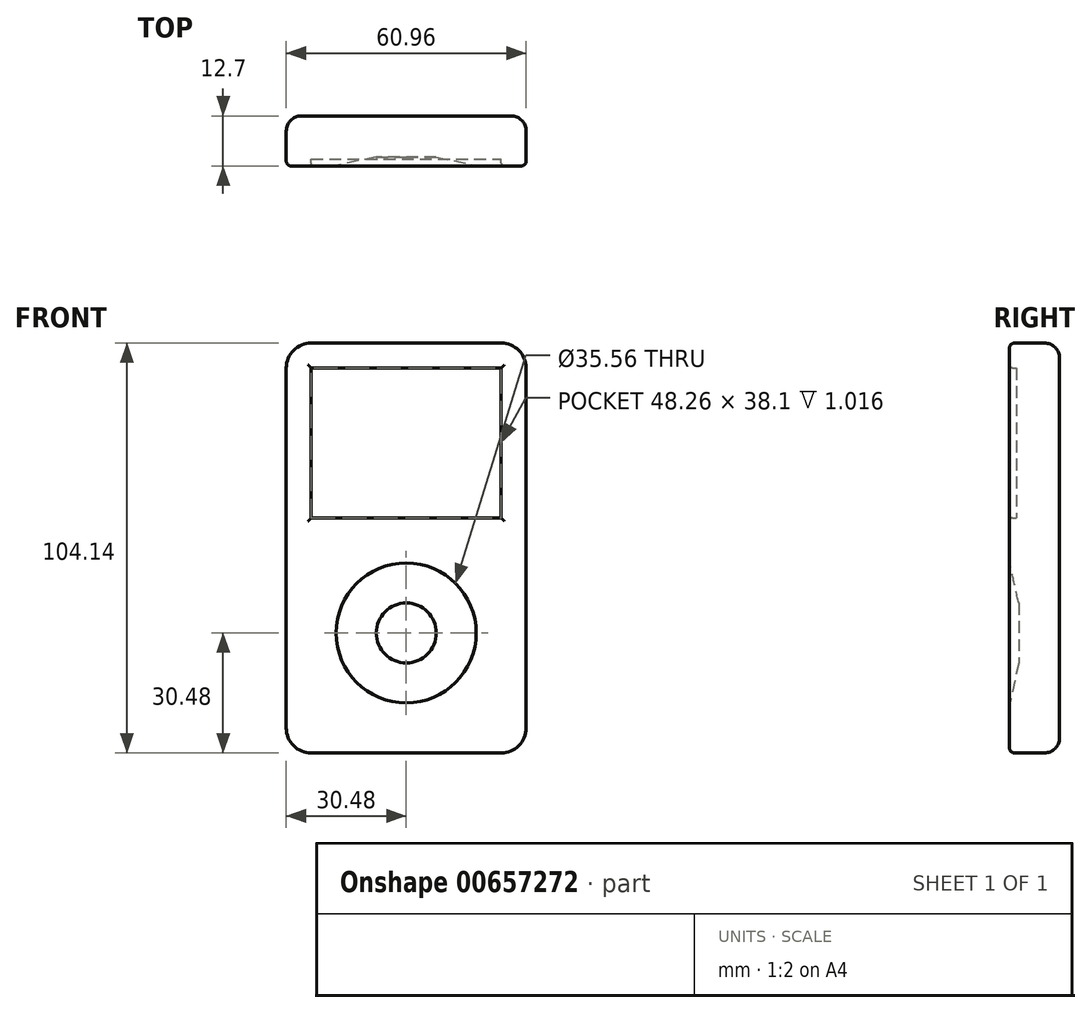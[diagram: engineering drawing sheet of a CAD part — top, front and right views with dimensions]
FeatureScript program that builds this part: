
annotation { "Feature Type Name" : "Feature", "Feature Type Description" : "" }
export const myFeature = defineFeature(function(context is Context, id is Id, definition is map)
    precondition{}
    {
        {
            var Q0;
            Q0=qCreatedBy(makeId("Front.planeOp"),FACE);
            var sketch = newSketch(context, id + "F0", { "sketchPlane" : qUnion([Q0])});
            skLineSegment(sketch, "E0.bottom", {"start": v(-24.13, 44.45) * mm, "end": v(24.13, 44.45) * mm});
            skLineSegment(sketch, "E0.top", {"start": v(-24.13, -59.69) * mm, "end": v(24.13, -59.69) * mm});
            skLineSegment(sketch, "E0.left", {"start": v(-30.48, 38.1) * mm, "end": v(-30.48, -53.34) * mm});
            skLineSegment(sketch, "E0.right", {"start": v(30.48, 38.1) * mm, "end": v(30.48, -53.34) * mm});
            skPoint(sketch, "E1.visualSharp", {"position": v(-30.48, 44.45) * mm});
            skArc(sketch, "E1.filletArc", {"start": v(-24.13, 44.45) * mm, "mid": v(-28.62, 42.6) * mm, "end": v(-30.48, 38.1) * mm});
            skPoint(sketch, "E2.visualSharp", {"position": v(30.48, 44.45) * mm});
            skArc(sketch, "E2.filletArc", {"start": v(30.48, 38.1) * mm, "mid": v(28.62, 42.6) * mm, "end": v(24.13, 44.45) * mm});
            skPoint(sketch, "E3.visualSharp", {"position": v(-30.48, -59.69) * mm});
            skArc(sketch, "E3.filletArc", {"start": v(-30.48, -53.34) * mm, "mid": v(-28.62, -57.83) * mm, "end": v(-24.13, -59.69) * mm});
            skPoint(sketch, "E4.visualSharp", {"position": v(30.48, -59.69) * mm});
            skArc(sketch, "E4.filletArc", {"start": v(24.13, -59.69) * mm, "mid": v(28.62, -57.83) * mm, "end": v(30.48, -53.34) * mm});
            skLineSegment(sketch, "E5.bottom", {"start": v(-24.13, 38.1) * mm, "end": v(24.13, 38.1) * mm});
            skLineSegment(sketch, "E5.top", {"start": v(-24.13, 0) * mm, "end": v(24.13, 0) * mm});
            skLineSegment(sketch, "E5.left", {"start": v(-24.13, 38.1) * mm, "end": v(-24.13, 0) * mm});
            skLineSegment(sketch, "E5.right", {"start": v(24.13, 38.1) * mm, "end": v(24.13, 0) * mm});
            skCircle(sketch, "E6", {"center": v(0, -29.2) * mm, "radius": 7.62 * mm});
            skCircle(sketch, "E7", {"center": v(0, -29.2) * mm, "radius": 17.78 * mm});
            skPoint(sketch, "E8", {"position": v(0, 44.45) * mm});
            skSolve(sketch);
        }
        {
            var Q0;
            Q0=makeQuery(id+"F0.imprint","IMPRINT",FACE,{"disambiguationData":[TD([[makeQuery(id+"F0.imprint","IMPRINT",EDGE,{"derivedFrom":sQuery(id+"F0.wireOp",EDGE,"E0.bottom")}),-1.0]])]});
            var Q1;
            Q1=makeQuery(id+"F0.imprint","IMPRINT",FACE,{"disambiguationData":[TD([[makeQuery(id+"F0.imprint","IMPRINT",EDGE,{"derivedFrom":sQuery(id+"F0.wireOp",EDGE,"E6")}),-1.0]])]});
            var Q2;
            Q2=makeQuery(id+"F0.imprint","IMPRINT",FACE,{"disambiguationData":[TD([[makeQuery(id+"F0.imprint","IMPRINT",EDGE,{"derivedFrom":sQuery(id+"F0.wireOp",EDGE,"E6")}),1.0]])]});
            extrude(context, id + "F1", {"entities" : qUnion([Q0, Q1, Q2]), "depth" : 12.7 * mm, "offsetDistance" : 25.4 * mm});
        }
        {
            var Q0;
            Q0=qCreatedBy(makeId("Front.planeOp"),FACE);
            var sketch = newSketch(context, id + "F2", { "sketchPlane" : qUnion([Q0])});
            skPoint(sketch, "E9", {"position": v(0, -29.13) * mm});
            skCircle(sketch, "E10", {"center": v(0, -29.13) * mm, "radius": 17.78 * mm});
            skCircle(sketch, "E11", {"center": v(0, -29.13) * mm, "radius": 7.62 * mm});
            skSolve(sketch);
        }
        {
            var Q0;
            Q0=qCreatedBy(makeId("Right.planeOp"),FACE);
            var sketch = newSketch(context, id + "F3", { "sketchPlane" : qUnion([Q0])});
            skLineSegment(sketch, "E12", {"start": v(-10.38, -29.21) * mm, "end": v(-5.66, -29.21) * mm});
            skLineSegment(sketch, "E13", {"start": v(-10.38, -29.21) * mm, "end": v(-10.38, -21.59) * mm});
            skLineSegment(sketch, "E14", {"start": v(-10.38, -21.59) * mm, "end": v(-12.64, -11.43) * mm});
            skLineSegment(sketch, "E15", {"start": v(-12.64, -11.43) * mm, "end": v(-38.04, -11.43) * mm});
            skLineSegment(sketch, "E16", {"start": v(-38.04, -29.21) * mm, "end": v(-5.66, -29.21) * mm});
            skLineSegment(sketch, "E17", {"start": v(-12.64, -11.43) * mm, "end": v(-16.62, -11.43) * mm});
            skLineSegment(sketch, "E18", {"start": v(-16.62, -11.43) * mm, "end": v(-16.62, -29.21) * mm});
            skLineSegment(sketch, "E19", {"start": v(-16.62, -29.21) * mm, "end": v(-10.38, -29.21) * mm});
            skSolve(sketch);
        }
        {
            var Q0;
            Q0 = qSketchRegion(id + "F3", true);
            var Q1;
            Q1=sQuery(id+"F3.wireOp",EDGE,"E12");
            revolve(context, id + "F4", {"operationType" : NewBodyOperationType.REMOVE, "entities" : qUnion([Q0]), "axis" : qUnion([Q1]), "revolveType" : RevolveType.FULL, "oppositeDirection" : true});
        }
        {
            var Q0;
            Q0=qCreatedBy(makeId("Front.planeOp"),FACE);
            var sketch = newSketch(context, id + "F5", { "sketchPlane" : qUnion([Q0])});
            skLineSegment(sketch, "E20.bottom", {"start": v(-24.13, 38.1) * mm, "end": v(24.13, 38.1) * mm});
            skLineSegment(sketch, "E20.top", {"start": v(-24.13, 0) * mm, "end": v(24.13, 0) * mm});
            skLineSegment(sketch, "E20.left", {"start": v(-24.13, 38.1) * mm, "end": v(-24.13, 0) * mm});
            skLineSegment(sketch, "E20.right", {"start": v(24.13, 38.1) * mm, "end": v(24.13, 0) * mm});
            skSolve(sketch);
        }
        {
            var Q0;
            Q0 = qSketchRegion(id + "F5", true);
            extrude(context, id + "F6", {"entities" : qUnion([Q0]), "operationType" : NewBodyOperationType.ADD, "depth" : 10.92 * mm, "offsetDistance" : 25.4 * mm});
        }
        {
            var Q0;
            Q0=makeQuery(id+"F1.opExtrude","CAP_EDGE",EDGE,{"disambiguationData":[OSD([sQuery(id+"F0.wireOp",EDGE,"E2.filletArc")])],"isStart":true});
            fillet(context, id + "F7", {"entities" : qUnion([Q0]), "radius" : 3.8 * mm, "tangentPropagation" : true, "allowEdgeOverflow" : false});
        }
        {
            var Q0;
            Q0=makeQuery(id+"F1.opExtrude","CAP_EDGE",EDGE,{"disambiguationData":[OSD([sQuery(id+"F0.wireOp",EDGE,"E2.filletArc")])],"isStart":false});
            fillet(context, id + "F8", {"entities" : qUnion([Q0]), "radius" : 1.27 * mm, "tangentPropagation" : true, "allowEdgeOverflow" : false});
        }
        {
            var Q0;
            Q0=makeQuery(id+"F1.opExtrude","CAP_EDGE",EDGE,{"disambiguationData":[OSD([sQuery(id+"F0.wireOp",EDGE,"E5.top")])],"isStart":false});
            var Q1;
            Q1=makeQuery(id+"F1.opExtrude","CAP_EDGE",EDGE,{"disambiguationData":[OSD([sQuery(id+"F0.wireOp",EDGE,"E5.left")])],"isStart":false});
            var Q2;
            Q2=makeQuery(id+"F1.opExtrude","CAP_EDGE",EDGE,{"disambiguationData":[OSD([sQuery(id+"F0.wireOp",EDGE,"E5.bottom")])],"isStart":false});
            var Q3;
            Q3=makeQuery(id+"F1.opExtrude","CAP_EDGE",EDGE,{"disambiguationData":[OSD([sQuery(id+"F0.wireOp",EDGE,"E5.right")])],"isStart":false});
            fillet(context, id + "F9", {"entities" : qUnion([Q0, Q1, Q2, Q3]), "radius" : 0.76 * mm, "tangentPropagation" : true, "allowEdgeOverflow" : false});
        }
    });
